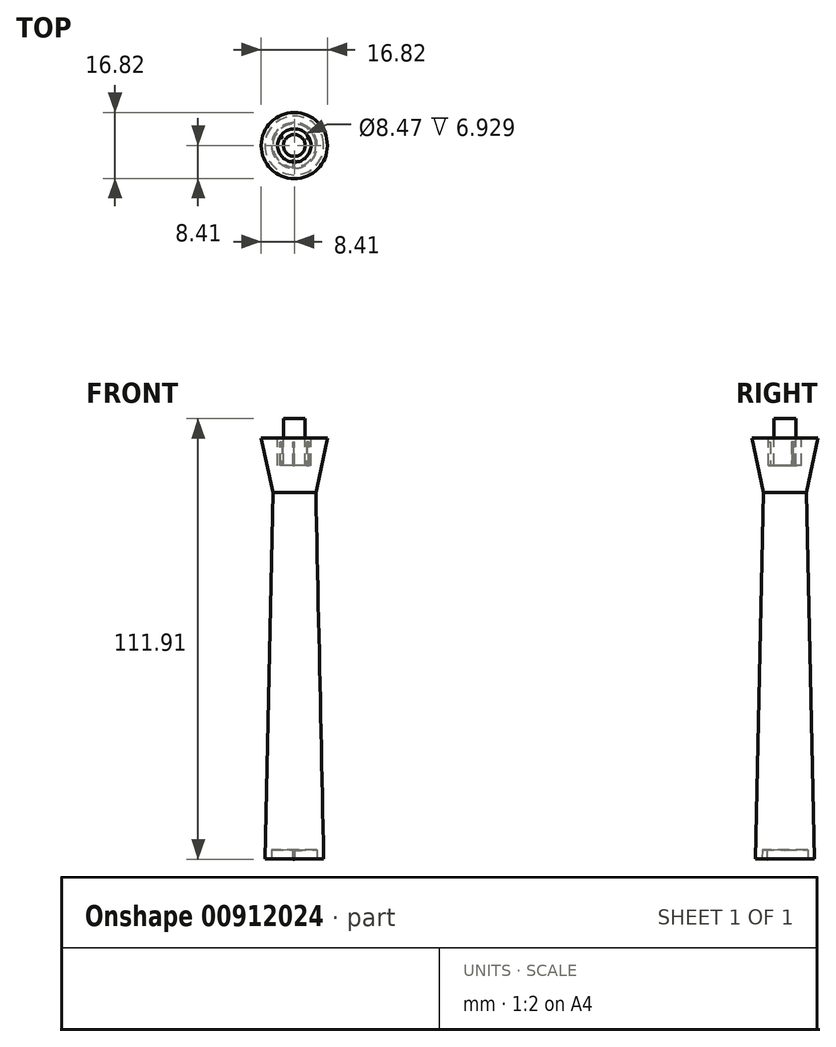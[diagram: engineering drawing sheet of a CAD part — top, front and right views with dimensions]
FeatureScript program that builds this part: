
annotation { "Feature Type Name" : "Feature", "Feature Type Description" : "" }
export const myFeature = defineFeature(function(context is Context, id is Id, definition is map)
    precondition{}
    {
        {
            var Q0;
            Q0=qCreatedBy(makeId("Front.planeOp"),FACE);
            var sketch = newSketch(context, id + "F0", { "sketchPlane" : qUnion([Q0])});
            skLineSegment(sketch, "E0", {"start": v(0, 56.94) * mm, "end": v(0, -52.73) * mm, "construction": true});
            skLineSegment(sketch, "E1", {"start": v(0, 56.94) * mm, "end": v(2.77, 56.94) * mm});
            skLineSegment(sketch, "E2", {"start": v(2.77, 56.94) * mm, "end": v(2.77, 45.09) * mm});
            skLineSegment(sketch, "E3", {"start": v(2.77, 45.09) * mm, "end": v(4.24, 45.09) * mm});
            skLineSegment(sketch, "E4", {"start": v(4.24, 45.09) * mm, "end": v(4.24, 52.02) * mm});
            skLineSegment(sketch, "E5", {"start": v(4.24, 52.02) * mm, "end": v(8.4, 52.02) * mm});
            skLineSegment(sketch, "E6", {"start": v(8.4, 52.02) * mm, "end": v(5.46, 38.16) * mm});
            skLineSegment(sketch, "E7", {"start": v(0, 56.94) * mm, "end": v(0, -52.73) * mm});
            skLineSegment(sketch, "E8", {"start": v(5.46, 38.16) * mm, "end": v(7.48, -54.9) * mm});
            skLineSegment(sketch, "E9", {"start": v(7.48, -54.9) * mm, "end": v(5.82, -54.94) * mm});
            skLineSegment(sketch, "E10", {"start": v(5.82, -54.94) * mm, "end": v(5.77, -52.6) * mm});
            skLineSegment(sketch, "E11", {"start": v(5.77, -52.6) * mm, "end": v(0, -52.73) * mm});
            skPoint(sketch, "E12", {"position": v(6.93, 45.09) * mm});
            skSolve(sketch);
        }
        {
            var Q0;
            Q0 = qSketchRegion(id + "F0", true);
            var Q1;
            Q1=sQuery(id+"F0.wireOp",EDGE,"E7");
            revolve(context, id + "F1", {"surfaceOperationType" : NewSurfaceOperationType.NEW, "entities" : qUnion([Q0]), "axis" : qUnion([Q1]), "revolveType" : RevolveType.FULL});
        }
        {
            var Q0;
            Q0=qCreatedBy(makeId("Right.planeOp"),FACE);
            var sketch = newSketch(context, id + "F2", { "sketchPlane" : qUnion([Q0])});
            skLineSegment(sketch, "E13", {"start": v(-4.2, 50.97) * mm, "end": v(-3.65, 50.97) * mm});
            skLineSegment(sketch, "E14", {"start": v(-3.65, 50.97) * mm, "end": v(-3.65, 45.06) * mm});
            skLineSegment(sketch, "E15", {"start": v(-3.65, 45.06) * mm, "end": v(-4.2, 45.06) * mm});
            skLineSegment(sketch, "E16", {"start": v(-4.2, 45.06) * mm, "end": v(-4.2, 50.97) * mm});
            skLineSegment(sketch, "E17", {"start": v(0, 58.29) * mm, "end": v(0, -72.7) * mm, "construction": true});
            skSolve(sketch);
        }
        {
            var Q0;
            Q0=qCreatedBy(makeId("Right.planeOp"),FACE);
            var sketch = newSketch(context, id + "F3", { "sketchPlane" : qUnion([Q0])});
            skLineSegment(sketch, "E18", {"start": v(-5.26, -52.6) * mm, "end": v(-5.78, -52.6) * mm});
            skLineSegment(sketch, "E19", {"start": v(-5.78, -52.6) * mm, "end": v(-5.85, -54.94) * mm});
            skLineSegment(sketch, "E20", {"start": v(-5.85, -54.94) * mm, "end": v(-4.53, -54.97) * mm});
            skLineSegment(sketch, "E21", {"start": v(-4.53, -54.97) * mm, "end": v(-4.46, -52.64) * mm});
            skLineSegment(sketch, "E22", {"start": v(-4.46, -52.64) * mm, "end": v(-5.26, -52.6) * mm});
            skSolve(sketch);
        }
        {
            var Q0;
            Q0 = qSketchRegion(id + "F2", true);
            var Q1;
            Q1=sQuery(id+"F2.wireOp",EDGE,"E17");
            revolve(context, id + "F4", {"surfaceOperationType" : NewSurfaceOperationType.NEW, "entities" : qUnion([Q0]), "axis" : qUnion([Q1]), "revolveType" : RevolveType.ONE_DIRECTION, "angle" : 4 * degree});
        }
        {
            var Q0;
            Q0=makeQuery(id+"F4.opRevolve","SWEPT_BODY",BODY,{"disambiguationData":[OSD([sQuery(id+"F2.wireOp",EDGE,"E13"),sQuery(id+"F2.wireOp",EDGE,"E14"),sQuery(id+"F2.wireOp",EDGE,"E15"),sQuery(id+"F2.wireOp",EDGE,"E16")])]});
            var Q1;
            Q1=sQuery(id+"F2.wireOp",EDGE,"E17");
            circularPattern(context, id + "F5", {"entities" : qUnion([Q0]), "axis" : qUnion([Q1]), "angle" : 360 * degree, "instanceCount" : 3, "equalSpace" : true});
        }
        {
            var Q0;
            Q0 = qSketchRegion(id + "F3", true);
            var Q1;
            Q1=sQuery(id+"F2.wireOp",EDGE,"E17");
            revolve(context, id + "F6", {"operationType" : NewBodyOperationType.ADD, "surfaceOperationType" : NewSurfaceOperationType.NEW, "entities" : qUnion([Q0]), "axis" : qUnion([Q1]), "revolveType" : RevolveType.ONE_DIRECTION, "angle" : 4 * degree});
        }
    });
